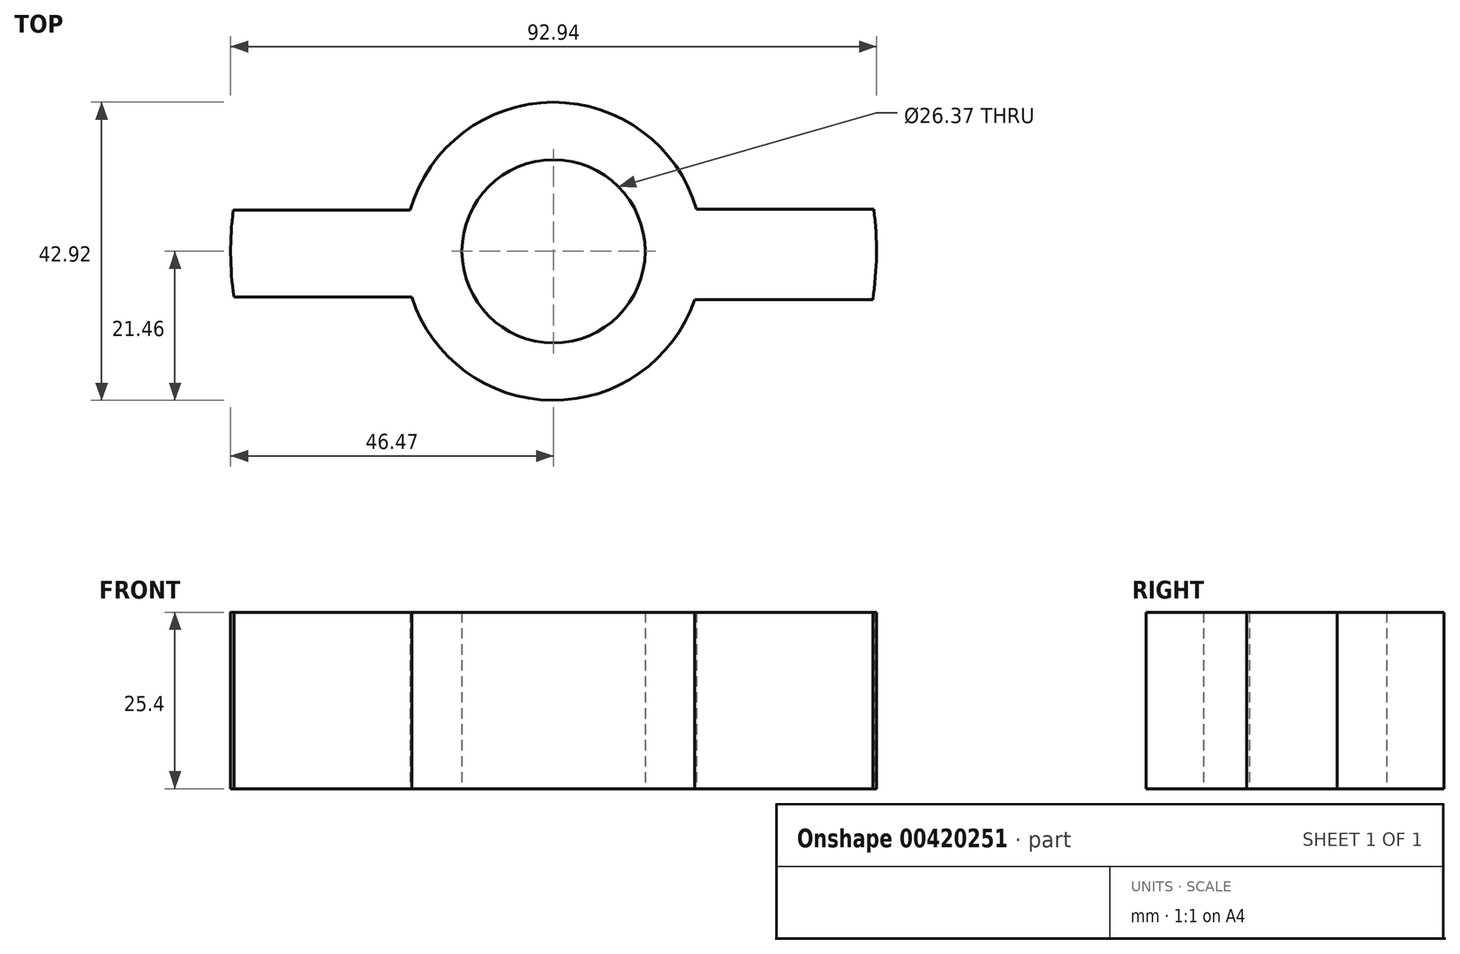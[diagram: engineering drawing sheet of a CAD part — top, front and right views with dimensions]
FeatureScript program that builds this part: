
annotation { "Feature Type Name" : "Feature", "Feature Type Description" : "" }
export const myFeature = defineFeature(function(context is Context, id is Id, definition is map)
    precondition{}
    {
        {
            var Q0;
            Q0=qCreatedBy(makeId("Top.planeOp"),FACE);
            var sketch = newSketch(context, id + "F0", { "sketchPlane" : qUnion([Q0])});
            skCircle(sketch, "E0", {"center": v(0, 0) * mm, "radius": 46.47 * mm});
            skCircle(sketch, "E1", {"center": v(0, 0) * mm, "radius": 13.18 * mm});
            skPoint(sketch, "E2.orphan", {"position": v(-46.47, 0) * mm});
            skCircle(sketch, "E3", {"center": v(0, 0) * mm, "radius": 21.46 * mm});
            skLineSegment(sketch, "E4", {"start": v(-46.09, 5.92) * mm, "end": v(-20.62, 5.92) * mm});
            skLineSegment(sketch, "E5", {"start": v(-46, -6.6) * mm, "end": v(-20.42, -6.6) * mm});
            skLineSegment(sketch, "E6", {"start": v(20.6, 6.03) * mm, "end": v(46.07, 6.03) * mm});
            skLineSegment(sketch, "E7", {"start": v(20.29, -6.98) * mm, "end": v(45.94, -6.98) * mm});
            skSolve(sketch);
        }
        {
            var Q0;
            {var subQ0=sQuery(id+"F0.wireOp",EDGE,"E4");Q0=makeQuery(id+"F0.imprint","IMPRINT",FACE,{"disambiguationData":[TD([[makeQuery(id+"F0.imprint","IMPRINT",EDGE,{"derivedFrom":subQ0}),-1.0]])]});}
            var Q1;
            {var subQ0=sQuery(id+"F0.wireOp",EDGE,"E6");Q1=makeQuery(id+"F0.imprint","IMPRINT",FACE,{"disambiguationData":[TD([[makeQuery(id+"F0.imprint","IMPRINT",EDGE,{"derivedFrom":subQ0}),-1.0]])]});}
            var Q2;
            Q2=makeQuery(id+"F0.imprint","IMPRINT",FACE,{"disambiguationData":[TD([[makeQuery(id+"F0.imprint","IMPRINT",EDGE,{"derivedFrom":sQuery(id+"F0.wireOp",EDGE,"E1")}),-1.0]])]});
            extrude(context, id + "F1", {"entities" : qUnion([Q0, Q1, Q2]), "depth" : 25.4 * mm});
        }
    });
